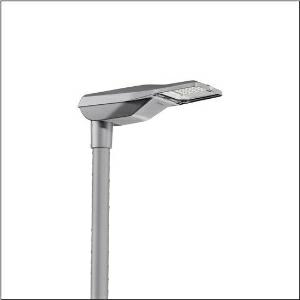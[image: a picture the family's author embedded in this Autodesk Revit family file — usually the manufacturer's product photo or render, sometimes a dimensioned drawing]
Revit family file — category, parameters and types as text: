
# Revit family: streetlight_sl_21_iq_micro___st1_0a_5xe1d31g08db_9cf9
name_source: partatom
category: Lighting Fixtures
units: mm (PartAtom-declared; Revit-internal decimal feet)

## family parameters
Cut with Voids When Loaded = No
Host = Face
Light Source = No
Part Type = Normal
Room Calculation Point = No
Round Connector Dimension = Use Diameter
Shared = No

## types (1)
- --- (1 x LED, 4810 lm, 36.4 W, 3000K)
    Apparent Load = 36 VA
    CIE Flux Codes = 37 72 97 100 100
    Color Rendering = 70
    Color Temperature = 3000K
    Default Elevation = 1800 mm
    Description = Streetlight SL 21 iQ micro, mast luminaire, primary light control with lens, of PMMA, primary optical cover: cover, of toughened safety glass, transparent, light distribution: ST1.0a, light emission: direct distribution, primary light characteristic: asymmetric, installation type: post-top, side-entry, LED, High Power LED, rated luminous flux: 4.810lm, luminous efficacy: 132lm/W, light colour: 730, colour temperature: 3000K, control gear: iQ Street-Remote, control: Street-Remote, Auto-Match, Temp-Guard, Lumen-Switch, Night-Set, Smart-Wire, Light-Fading, Desk-Remote (wireless, voltage-free reading and setting of iQ features in the workshop via application-optimized NFC function/RFID function), optimised constant luminous flux control (CLO 2.0), pre-setting: linear dimming characteristic, mains connection: 220..240V, AC, 50/60Hz, start of lifetime: 36W, end of service life: 38W, reduction: 16W, luminaire housing, of diecast aluminium, powder-coated, Siteco® metallic grey (DB 702S), corrosivity category C5 mid according to DIN EN ISO 12944, please order mast flange separately, inclination adjustable: 0°, 5°, 10°, 15°, sealing non-destructively replaceable, multi-level sealing system, length: 528mm, width: 235mm, height: 110mm, mast flange for spigot size: 42mm (side-entry): 5XC10008XM4, 60/48mm (side-entry/post-top): 5XC10108XM2, 76/60mm (side-entry/post-top): 5XC10108XM1, protection rating (complete): IP66, insulation class (complete): insulation class II (safety insulation), certification: CE, ENEC, ENEC+, VDE, impact resistance: IK10, permissible operating ambient temperature for outdoor applications: -40..+50°C, standard-compliant lighting for roads and squares, packaging unit: 1 piece

Light Distribution: ST1.0a
    Height = 110 mm
    Lamp = 1 x LED
    Lamp Light Flux = 4810 lm
    Lamp Power = 36.4 W
    Lamp count = 1
    Length = 528 mm
    Luminous efficacy = 132 lm/W
    Manufacturer = Siteco
    ModVariant = No
    Model = 5XE1D31G08DB
    Number of Poles = 1
    OnlyDefault = Yes
    Power Factor = 1
    Product Name = Streetlight SL 21 iQ micro | ST1.0a
    Product group = mast luminaire | pylon top
    ProductGroupID = 6100
    Protection Class = Protection class II
    Protection Degree = IP 66
    RLX_Detail_Level = 1
    RLX_Emergency_Light_Flux = 0 lm
    RLX_Emergency_Type = 0
    RLX_Emergency_Type_DB = No
    RlxData = <blob elided: 98765 chars, md5=00b0f3c1>
    Socket = socket
    Standby Power = 0 W
    System Light Flux = 4810 lm
    System Power = 36 W
    Type Comments = factory setting: luminous flux: 100 % | dim-lin: 254 | 715 mA
    Type Image = l_1006881.jpg
    URL = http://relux.com
    VarID = @adj_156026
    Voltage = 0 V
    Weight = 0.00 kg
    Width = 235 mm

## geometry (parser evidence)
native form markers: Blend x4, Sweep x12
no freeform markers — native parametric forms only
